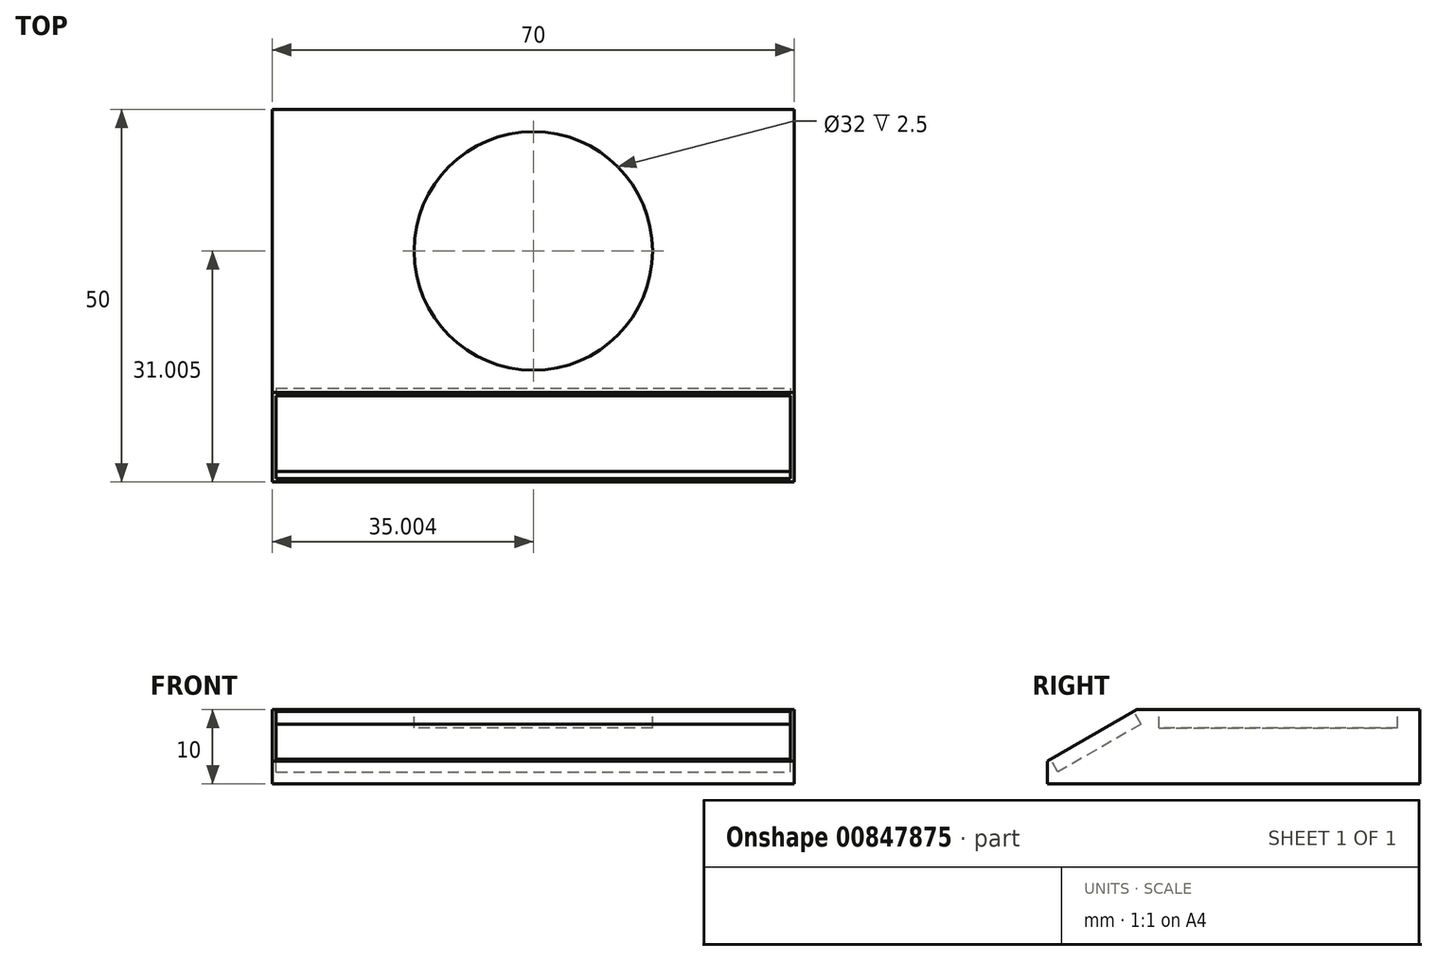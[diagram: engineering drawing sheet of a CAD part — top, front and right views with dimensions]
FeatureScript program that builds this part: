
annotation { "Feature Type Name" : "Feature", "Feature Type Description" : "" }
export const myFeature = defineFeature(function(context is Context, id is Id, definition is map)
    precondition{}
    {
        {
            var Q0;
            Q0=qCreatedBy(makeId("Top.planeOp"),FACE);
            var sketch = newSketch(context, id + "F0", { "sketchPlane" : qUnion([Q0])});
            skLineSegment(sketch, "E0.bottom", {"start": v(-29.86, 30.26) * mm, "end": v(40.14, 30.26) * mm});
            skLineSegment(sketch, "E0.top", {"start": v(-29.86, -19.74) * mm, "end": v(40.14, -19.74) * mm});
            skLineSegment(sketch, "E0.left", {"start": v(-29.86, 30.26) * mm, "end": v(-29.86, -19.74) * mm});
            skLineSegment(sketch, "E0.right", {"start": v(40.14, 30.26) * mm, "end": v(40.14, -19.74) * mm});
            skSolve(sketch);
        }
        {
            var Q0;
            Q0=makeQuery(id+"F0.imprint","IMPRINT",FACE,{"disambiguationData":[TD([[makeQuery(id+"F0.imprint","IMPRINT",EDGE,{"derivedFrom":sQuery(id+"F0.wireOp",EDGE,"E0.bottom")}),-1.0]])]});
            extrude(context, id + "F1", {"entities" : qUnion([Q0]), "depth" : 10 * mm, "offsetDistance" : 25 * mm});
        }
        {
            var Q0;
            Q0=makeQuery(id+"F1.opExtrude","CAP_EDGE",EDGE,{"disambiguationData":[OSD([sQuery(id+"F0.wireOp",EDGE,"E0.top")])],"isStart":false});
            chamfer(context, id + "F2", {"entities" : qUnion([Q0]), "chamferType" : ChamferType.OFFSET_ANGLE, "width" : 12 * mm, "oppositeDirection" : false, "angle" : 30 * degree, "tangentPropagation" : true});
        }
        {
            var Q0;
            Q0=makeQuery(id+"F1.opExtrude","CAP_FACE",FACE,{"disambiguationData":[OSD([sQuery(id+"F0.wireOp",EDGE,"E0.bottom"),sQuery(id+"F0.wireOp",EDGE,"E0.top"),sQuery(id+"F0.wireOp",EDGE,"E0.left"),sQuery(id+"F0.wireOp",EDGE,"E0.right")])],"isStart":false});
            var sketch = newSketch(context, id + "F3", { "sketchPlane" : qUnion([Q0])});
            skCircle(sketch, "E1", {"center": v(5.14, 11.26) * mm, "radius": 16 * mm});
            skSolve(sketch);
        }
        {
            var Q0;
            Q0=qSketchRegion(id+"F3",true);
            extrude(context, id + "F4", {"entities" : qUnion([Q0]), "operationType" : NewBodyOperationType.REMOVE, "oppositeDirection" : true, "depth" : 2.5 * mm, "offsetDistance" : 25 * mm});
        }
        {
            var Q0;
            Q0=makeQuery(id+"F2.opChamfer","BLEND_FACE",FACE,{"disambiguationData":[OSD([sQuery(id+"F0.wireOp",EDGE,"E0.top")])]});
            var sketch = newSketch(context, id + "F5", { "sketchPlane" : qUnion([Q0])});
            skLineSegment(sketch, "E2.bottom", {"start": v(-29.36, -2.2) * mm, "end": v(39.64, -2.2) * mm});
            skLineSegment(sketch, "E2.top", {"start": v(-29.36, -15.06) * mm, "end": v(39.64, -15.06) * mm});
            skLineSegment(sketch, "E2.left", {"start": v(-29.36, -2.2) * mm, "end": v(-29.36, -15.06) * mm});
            skLineSegment(sketch, "E2.right", {"start": v(39.64, -2.2) * mm, "end": v(39.64, -15.06) * mm});
            skSolve(sketch);
        }
        {
            var Q0;
            Q0=qSketchRegion(id+"F5",true);
            extrude(context, id + "F6", {"entities" : qUnion([Q0]), "operationType" : NewBodyOperationType.REMOVE, "depth" : -2 * mm, "hasOffset" : true, "offsetDistance" : -1 * mm});
        }
    });
